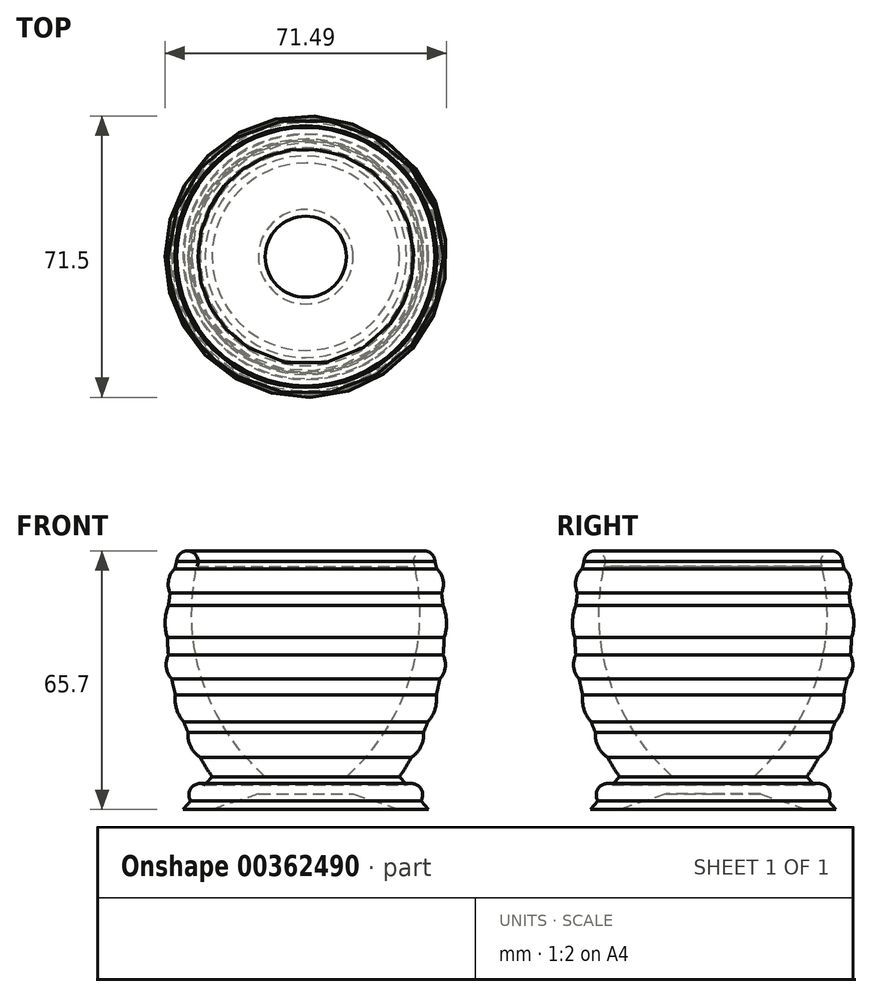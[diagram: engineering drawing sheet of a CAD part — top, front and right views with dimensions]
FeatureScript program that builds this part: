
annotation { "Feature Type Name" : "Feature", "Feature Type Description" : "" }
export const myFeature = defineFeature(function(context is Context, id is Id, definition is map)
    precondition{}
    {
        {
            var Q0;
            Q0=qCreatedBy(makeId("Front.planeOp"),FACE);
            var sketch = newSketch(context, id + "F0", { "sketchPlane" : qUnion([Q0])});
            skLineSegment(sketch, "E0", {"start": v(-19.28, 8.35) * mm, "end": v(-10.02, 8.35) * mm});
            skLineSegment(sketch, "E1", {"start": v(-32.79, 0) * mm, "end": v(-21, 3.95) * mm});
            skLineSegment(sketch, "E2", {"start": v(-21, 3.95) * mm, "end": v(-8.97, 3.95) * mm});
            skLineSegment(sketch, "E3", {"start": v(-8.97, 3.95) * mm, "end": v(-8.97, 8.35) * mm});
            skLineSegment(sketch, "E4", {"start": v(-8.97, 8.35) * mm, "end": v(-10.02, 8.35) * mm});
            skArc(sketch, "E5", {"start": v(-36.66, 61.76) * mm, "mid": v(-38.43, 65.62) * mm, "end": v(-41.77, 63) * mm});
            skArc(sketch, "E6", {"start": v(-36.66, 61.76) * mm, "mid": v(-35.24, 32.68) * mm, "end": v(-19.28, 8.35) * mm});
            skLineSegment(sketch, "E7", {"start": v(-32.79, 0) * mm, "end": v(-40.17, 0) * mm});
            skLineSegment(sketch, "E8", {"start": v(-40.17, 0) * mm, "end": v(-38.22, 2.2) * mm});
            skArc(sketch, "E9", {"start": v(-41.77, 63) * mm, "mid": v(-42.01, 62.09) * mm, "end": v(-42.24, 61.17) * mm});
            skArc(sketch, "E10", {"start": v(-42.24, 61.17) * mm, "mid": v(-43.83, 58.3) * mm, "end": v(-43.45, 55.04) * mm});
            skArc(sketch, "E11", {"start": v(-43.83, 51.9) * mm, "mid": v(-44.71, 47.8) * mm, "end": v(-44.13, 43.67) * mm});
            skPoint(sketch, "E11.startSnap0", {"position": v(-43.83, 58.3) * mm});
            skArc(sketch, "E12", {"start": v(-43.87, 39.28) * mm, "mid": v(-44.4, 36.09) * mm, "end": v(-43, 33.17) * mm});
            skArc(sketch, "E13", {"start": v(-42.13, 29.17) * mm, "mid": v(-41.79, 25.46) * mm, "end": v(-39.95, 22.21) * mm});
            skArc(sketch, "E14", {"start": v(-38.89, 19.55) * mm, "mid": v(-38.22, 15.99) * mm, "end": v(-35.82, 13.28) * mm});
            skArc(sketch, "E15", {"start": v(-34.6, 6.3) * mm, "mid": v(-37.96, 5.63) * mm, "end": v(-38.22, 2.2) * mm});
            skPoint(sketch, "E15.endSnap0", {"position": v(-38.22, 15.99) * mm});
            skArc(sketch, "E16.trimOffspring", {"start": v(-43.45, 55.04) * mm, "mid": v(-43.66, 53.47) * mm, "end": v(-43.83, 51.9) * mm});
            skArc(sketch, "E17.trimOffspring", {"start": v(-44.13, 43.67) * mm, "mid": v(-44.03, 41.47) * mm, "end": v(-43.87, 39.28) * mm});
            skArc(sketch, "E18.trimOffspring", {"start": v(-43, 33.17) * mm, "mid": v(-42.6, 31.16) * mm, "end": v(-42.13, 29.17) * mm});
            skArc(sketch, "E19.trimOffspring", {"start": v(-39.95, 22.21) * mm, "mid": v(-39.43, 20.88) * mm, "end": v(-38.89, 19.55) * mm});
            skArc(sketch, "E20.trimOffspring", {"start": v(-35.82, 13.28) * mm, "mid": v(-34.36, 10.78) * mm, "end": v(-32.79, 8.35) * mm});
            skLineSegment(sketch, "E21.trimOffspring", {"start": v(-34.6, 6.3) * mm, "end": v(-32.79, 8.35) * mm});
            skSolve(sketch);
        }
        {
            var Q0;
            Q0 = qSketchRegion(id + "F0", true);
            var Q1;
            Q1=sQuery(id+"F0.wireOp",EDGE,"E3");
            revolve(context, id + "F1", {"entities" : qUnion([Q0]), "axis" : qUnion([Q1]), "revolveType" : RevolveType.FULL});
        }
    });
